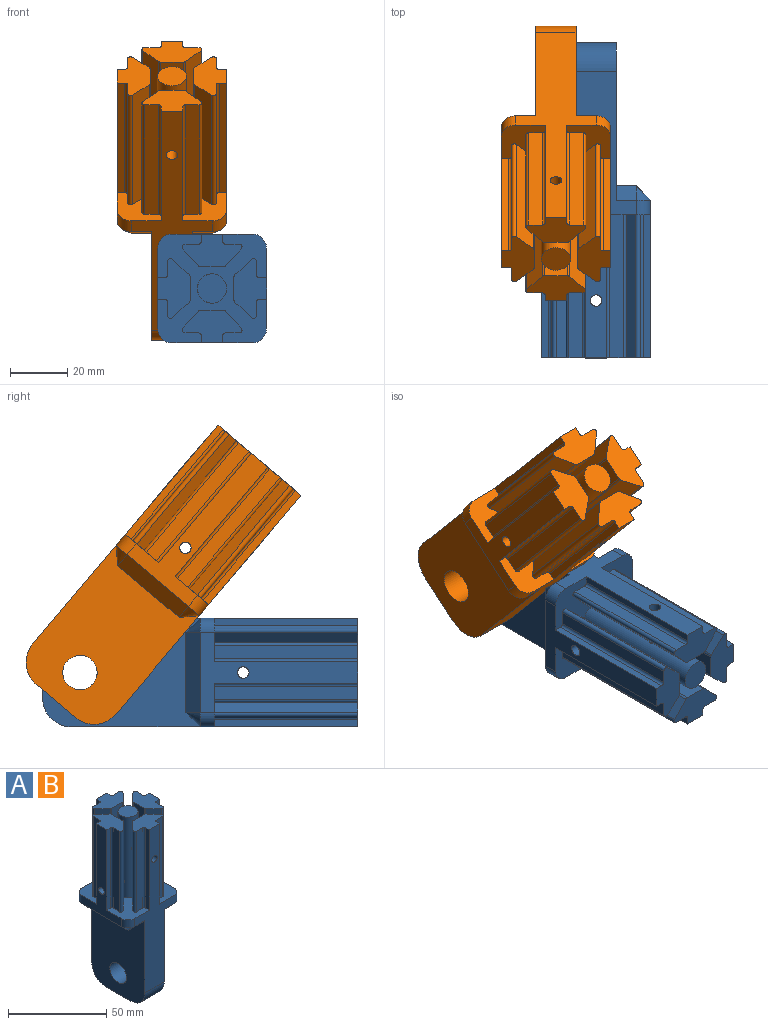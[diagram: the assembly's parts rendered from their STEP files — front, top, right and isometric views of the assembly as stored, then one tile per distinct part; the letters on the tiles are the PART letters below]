
ASSEMBLY  parts=2 mates=1
PART A: 91 faces, bbox 38x38x110 mm
  f0: plane 28x7mm, normal (0,0,-1), area 196mm2, adj f75,f81,f83,f85
  f1: plane 28x7mm, normal (0,0,-1), area 196mm2, adj f76,f86,f88,f90
  f2: plane 38x38mm, normal (0,0,1), area 732.4mm2, adj f3,f4,f5,f6,f7,f8,f9,f10
  f3: cylinder r=5mm len=5mm, axis (0,0,1), area 39.3mm2, adj f2,f4,f10,f84
  f4: plane 100x28mm, normal (0,-1,0), area 1132.4mm2, adj f2,f3,f5,f11,f23,f24,f74,f75
  f5: cylinder r=5mm len=5mm, axis (0,0,1), area 39.3mm2, adj f2,f4,f6,f89
  f6: plane 55x28mm, normal (1,0,0), area 502.4mm2, adj f2,f5,f7,f36,f37,f38,f71,f88
  f7: cylinder r=5mm len=5mm, axis (0,0,1), area 39.3mm2, adj f2,f6,f8,f87
  f8: plane 100x28mm, normal (0,1,0), area 1132.4mm2, adj f2,f7,f9,f41,f42,f52,f73,f75
  f9: cylinder r=5mm len=5mm, axis (0,0,1), area 39.3mm2, adj f2,f8,f10,f82
  f10: plane 55x28mm, normal (-1,0,0), area 502.4mm2, adj f2,f3,f9,f55,f56,f66,f70,f83
  f11: plane 50x2.5mm, normal (1,0,0), area 125mm2, adj f2,f4,f12,f24
  f12: cylinder r=1mm len=50mm, axis (0,0,-1), area 78.5mm2, adj f2,f11,f13,f24
  f13: plane 50x4.7mm, normal (0,-1,0), area 235.2mm2, adj f2,f12,f14,f24
  f14: cylinder r=1mm len=50mm, axis (0,0,-1), area 115.9mm2, adj f2,f13,f15,f24
  f15: plane 50x5.9mm, normal (0.73,0.68,0), area 402mm2, adj f2,f14,f16,f24
  f16: cylinder r=1mm len=50mm, axis (0,0,-1), area 41.2mm2, adj f2,f15,f17,f24
  f17: plane 50x7.98mm, normal (0,1,0), area 386.5mm2, adj f2,f16,f18,f24,f74
  f18: cylinder r=1mm len=50mm, axis (0,0,-1), area 41.2mm2, adj f2,f17,f19,f24
  f19: plane 50x5.9mm, normal (-0.73,0.68,0), area 402mm2, adj f2,f18,f20,f24
  f20: cylinder r=1mm len=50mm, axis (0,0,-1), area 115.9mm2, adj f2,f19,f21,f24
  f21: plane 50x4.7mm, normal (0,-1,0), area 235.2mm2, adj f2,f20,f22,f24
  f22: cylinder r=1mm len=50mm, axis (0,0,-1), area 78.5mm2, adj f2,f21,f23,f24
  f23: plane 50x2.5mm, normal (-1,0,0), area 125mm2, adj f2,f4,f22,f24
  f24: plane 20.91x11.4mm, normal (0,0,1), area 152.1mm2, adj f4,f11,f12,f13,f14,f15,f16,f17
  f25: cylinder r=1mm len=50mm, axis (0,0,-1), area 78.5mm2, adj f2,f26,f37,f38
  f26: plane 50x4.7mm, normal (1,0,0), area 235.2mm2, adj f2,f25,f27,f38
  f27: cylinder r=1mm len=50mm, axis (0,0,-1), area 116mm2, adj f2,f26,f28,f38
  f28: plane 50x5.9mm, normal (-0.68,0.73,0), area 401.9mm2, adj f2,f27,f29,f38
  f29: cylinder r=1mm len=50mm, axis (0,0,-1), area 41.2mm2, adj f2,f28,f30,f38
  f30: plane 50x7.98mm, normal (-1,0,0), area 386.5mm2, adj f2,f29,f31,f38,f71
  f31: cylinder r=1mm len=50mm, axis (0,0,-1), area 41.2mm2, adj f2,f30,f32,f38
  f32: plane 50x5.9mm, normal (-0.68,-0.73,0), area 401.9mm2, adj f2,f31,f33,f38
  f33: cylinder r=1mm len=50mm, axis (0,0,-1), area 116mm2, adj f2,f32,f34,f38
  f34: plane 50x4.7mm, normal (1,0,0), area 235.2mm2, adj f2,f33,f35,f38
  f35: cylinder r=1mm len=50mm, axis (0,0,-1), area 78.5mm2, adj f2,f34,f36,f38
  f36: plane 50x2.5mm, normal (0,-1,0), area 125mm2, adj f2,f6,f35,f38
  f37: plane 50x2.5mm, normal (0,1,0), area 125mm2, adj f2,f6,f25,f38
  f38: plane 20.91x11.4mm, normal (0,0,1), area 152.1mm2, adj f6,f25,f26,f27,f28,f29,f30,f31
  f39: plane 50x4.7mm, normal (0,1,0), area 235.2mm2, adj f2,f40,f51,f52
  f40: cylinder r=1mm len=50mm, axis (0,0,-1), area 78.5mm2, adj f2,f39,f41,f52
  f41: plane 50x2.5mm, normal (1,0,0), area 125mm2, adj f2,f8,f40,f52
  f42: plane 50x2.5mm, normal (-1,0,0), area 125mm2, adj f2,f8,f43,f52
  f43: cylinder r=1mm len=50mm, axis (0,0,-1), area 78.5mm2, adj f2,f42,f44,f52
  f44: plane 50x4.7mm, normal (0,1,0), area 235.2mm2, adj f2,f43,f45,f52
  f45: cylinder r=1mm len=50mm, axis (0,0,-1), area 115.9mm2, adj f2,f44,f46,f52
  f46: plane 50x5.9mm, normal (-0.73,-0.68,0), area 402mm2, adj f2,f45,f47,f52
  f47: cylinder r=1mm len=50mm, axis (0,0,-1), area 41.2mm2, adj f2,f46,f48,f52
  f48: plane 50x7.98mm, normal (0,-1,0), area 386.5mm2, adj f2,f47,f49,f52,f73
  f49: cylinder r=1mm len=50mm, axis (0,0,-1), area 41.2mm2, adj f2,f48,f50,f52
  f50: plane 50x5.9mm, normal (0.73,-0.68,0), area 402mm2, adj f2,f49,f51,f52
  f51: cylinder r=1mm len=50mm, axis (0,0,-1), area 115.9mm2, adj f2,f39,f50,f52
  f52: plane 20.91x11.4mm, normal (0,0,1), area 152.1mm2, adj f8,f39,f40,f41,f42,f43,f44,f45
  f53: plane 50x4.7mm, normal (-1,0,0), area 235.2mm2, adj f2,f54,f65,f66
  f54: cylinder r=1mm len=50mm, axis (0,0,-1), area 78.5mm2, adj f2,f53,f55,f66
  f55: plane 50x2.5mm, normal (0,1,0), area 125mm2, adj f2,f10,f54,f66
  f56: plane 50x2.5mm, normal (0,-1,0), area 125mm2, adj f2,f10,f57,f66
  f57: cylinder r=1mm len=50mm, axis (0,0,-1), area 78.5mm2, adj f2,f56,f58,f66
  f58: plane 50x4.7mm, normal (-1,0,0), area 235.2mm2, adj f2,f57,f59,f66
  f59: cylinder r=1mm len=50mm, axis (0,0,-1), area 116mm2, adj f2,f58,f60,f66
  f60: plane 50x5.9mm, normal (0.68,-0.73,0), area 401.9mm2, adj f2,f59,f61,f66
  f61: cylinder r=1mm len=50mm, axis (0,0,-1), area 41.2mm2, adj f2,f60,f62,f66
  f62: plane 50x7.98mm, normal (1,0,0), area 386.5mm2, adj f2,f61,f63,f66,f70
  f63: cylinder r=1mm len=50mm, axis (0,0,-1), area 41.2mm2, adj f2,f62,f64,f66
  f64: plane 50x5.9mm, normal (0.68,0.73,0), area 401.9mm2, adj f2,f63,f65,f66
  f65: cylinder r=1mm len=50mm, axis (0,0,-1), area 116mm2, adj f2,f53,f64,f66
  f66: plane 20.91x11.4mm, normal (0,0,1), area 152.1mm2, adj f10,f53,f54,f55,f56,f57,f58,f59
  f67: cylinder r=5.1mm len=50mm, axis (0,0,-1), area 1551mm2, adj f2,f68,f69,f72
  f68: plane 10.2x10.2mm, normal (0,0,1), area 81.7mm2, adj f67
  f69: cylinder r=2mm len=10.2mm, axis (1,0,0), area 123.1mm2, adj f67
  f70: cylinder r=2mm len=11.4mm, axis (1,0,0), area 143.3mm2, adj f10,f62
  f71: cylinder r=2mm len=11.4mm, axis (1,0,0), area 143.3mm2, adj f6,f30
  f72: cylinder r=2mm len=10.2mm, axis (0,-1,0), area 123.1mm2, adj f67
  f73: cylinder r=2mm len=11.4mm, axis (0,-1,0), area 143.3mm2, adj f8,f48
  f74: cylinder r=2mm len=11.4mm, axis (0,-1,0), area 143.3mm2, adj f4,f17
  f75: plane 55x38mm, normal (-1,0,0), area 1769mm2, adj f0,f4,f8,f77,f78,f79,f80,f81
  f76: plane 55x38mm, normal (1,0,0), area 1769mm2, adj f1,f4,f8,f77,f78,f79,f80,f86
  f77: plane 18x14mm, normal (0,0,-1), area 252mm2, adj f75,f76,f79,f80
  f78: cylinder r=6mm len=14mm, axis (1,0,0), area 527.8mm2, adj f75,f76
  f79: cylinder r=10mm len=14mm, axis (1,0,0), area 219.9mm2, adj f4,f75,f76,f77
  f80: cylinder r=10mm len=14mm, axis (-1,0,0), area 219.9mm2, adj f8,f75,f76,f77
  f81: plane 7x5mm, normal (0,0.71,-0.71), area 49.5mm2, adj f0,f8,f75,f82
  f82: cone r=5mm half-angle=45deg, axis (0,0,1), area 27.8mm2, adj f9,f81,f83
  f83: plane 28x5mm, normal (-0.71,0,-0.71), area 198mm2, adj f0,f10,f82,f84
  f84: cone r=5mm half-angle=45deg, axis (0,0,1), area 27.8mm2, adj f3,f83,f85
  f85: plane 7x5mm, normal (0,-0.71,-0.71), area 49.5mm2, adj f0,f4,f75,f84
  f86: plane 7x5mm, normal (0,0.71,-0.71), area 49.5mm2, adj f1,f8,f76,f87
  f87: cone r=5mm half-angle=45deg, axis (0,0,1), area 27.8mm2, adj f7,f86,f88
  f88: plane 28x5mm, normal (0.71,0,-0.71), area 198mm2, adj f1,f6,f87,f89
  f89: cone r=5mm half-angle=45deg, axis (0,0,1), area 27.8mm2, adj f5,f88,f90
  f90: plane 7x5mm, normal (0,-0.71,-0.71), area 49.5mm2, adj f1,f4,f76,f89
PART B: same geometry as A
PLACE A rot(axis=(1,0,0),90deg) t=(-3.35,-1.76,24.44)mm
PLACE B rot(axis=(1,0,0),40.2deg) t=(-17.35,-18.97,76.05)mm
MATE cylindrical B.f78 <-> A.f78  axis (1,0,0) through (97.2,45.24,68.79)mm
